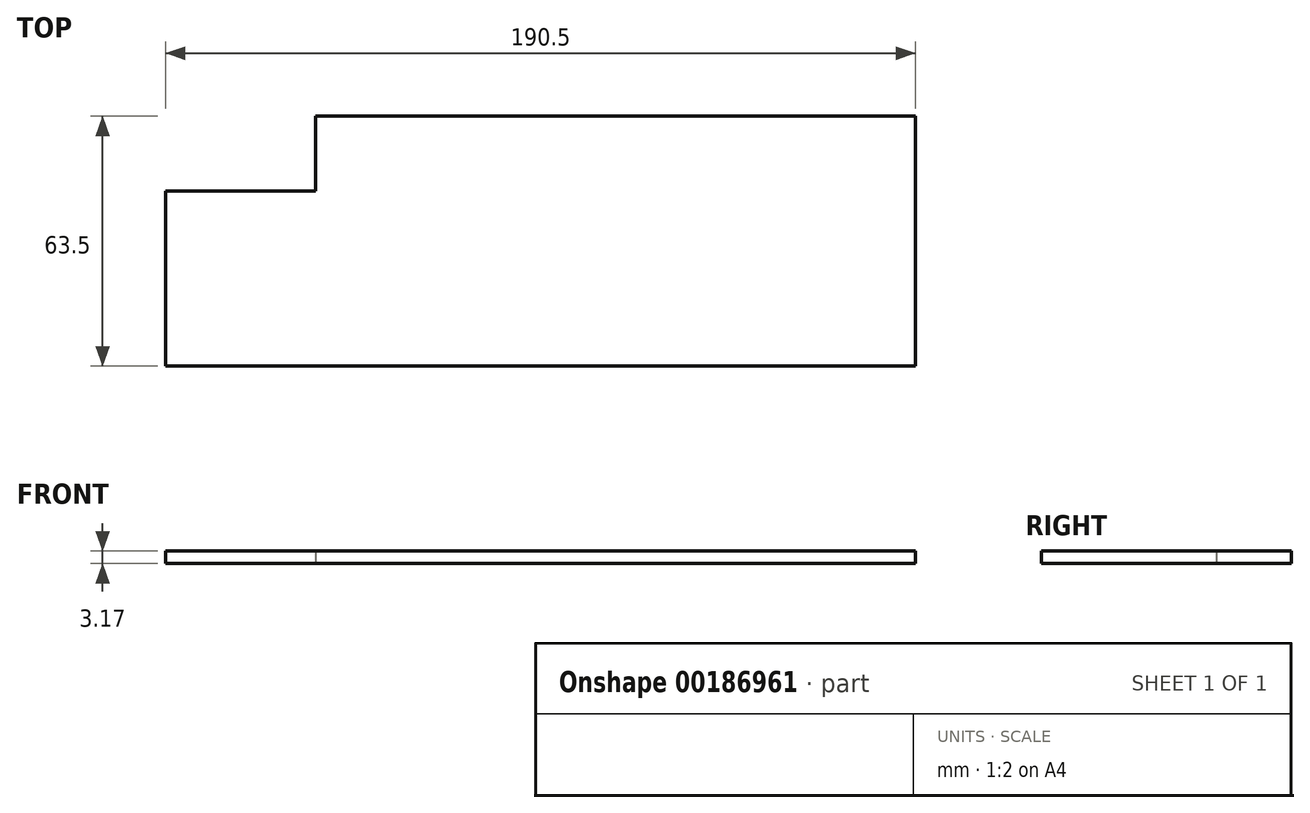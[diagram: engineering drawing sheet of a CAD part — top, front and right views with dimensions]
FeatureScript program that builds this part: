
annotation { "Feature Type Name" : "Feature", "Feature Type Description" : "" }
export const myFeature = defineFeature(function(context is Context, id is Id, definition is map)
    precondition{}
    {
        {
            var Q0;
            Q0=qCreatedBy(makeId("Top.planeOp"),FACE);
            var sketch = newSketch(context, id + "F0", { "sketchPlane" : qUnion([Q0])});
            skLineSegment(sketch, "E0.bottom", {"start": v(95.25, -31.75) * mm, "end": v(-95.25, -31.75) * mm});
            skLineSegment(sketch, "E0.top", {"start": v(95.25, 31.75) * mm, "end": v(-57.15, 31.75) * mm});
            skLineSegment(sketch, "E0.left", {"start": v(95.25, -31.75) * mm, "end": v(95.25, 31.75) * mm});
            skPoint(sketch, "E0.middle", {"position": v(0, 0) * mm});
            skPoint(sketch, "E1.orphan", {"position": v(-95.25, 31.75) * mm});
            skLineSegment(sketch, "E2", {"start": v(-57.15, 31.75) * mm, "end": v(-57.15, 12.7) * mm});
            skLineSegment(sketch, "E3", {"start": v(-57.15, 12.7) * mm, "end": v(-95.25, 12.7) * mm});
            skPoint(sketch, "E4.orphan", {"position": v(-95.25, 0) * mm});
            skLineSegment(sketch, "E5", {"start": v(-95.25, 12.7) * mm, "end": v(-95.25, -31.75) * mm});
            skSolve(sketch);
        }
        {
            var Q0;
            Q0=makeQuery(id+"F0.imprint","IMPRINT",FACE,{"disambiguationData":[TD([[makeQuery(id+"F0.imprint","IMPRINT",EDGE,{"derivedFrom":sQuery(id+"F0.wireOp",EDGE,"E0.bottom")}),-1.0]])]});
            extrude(context, id + "F1", {"entities" : qUnion([Q0]), "depth" : 3.17 * mm});
        }
    });
